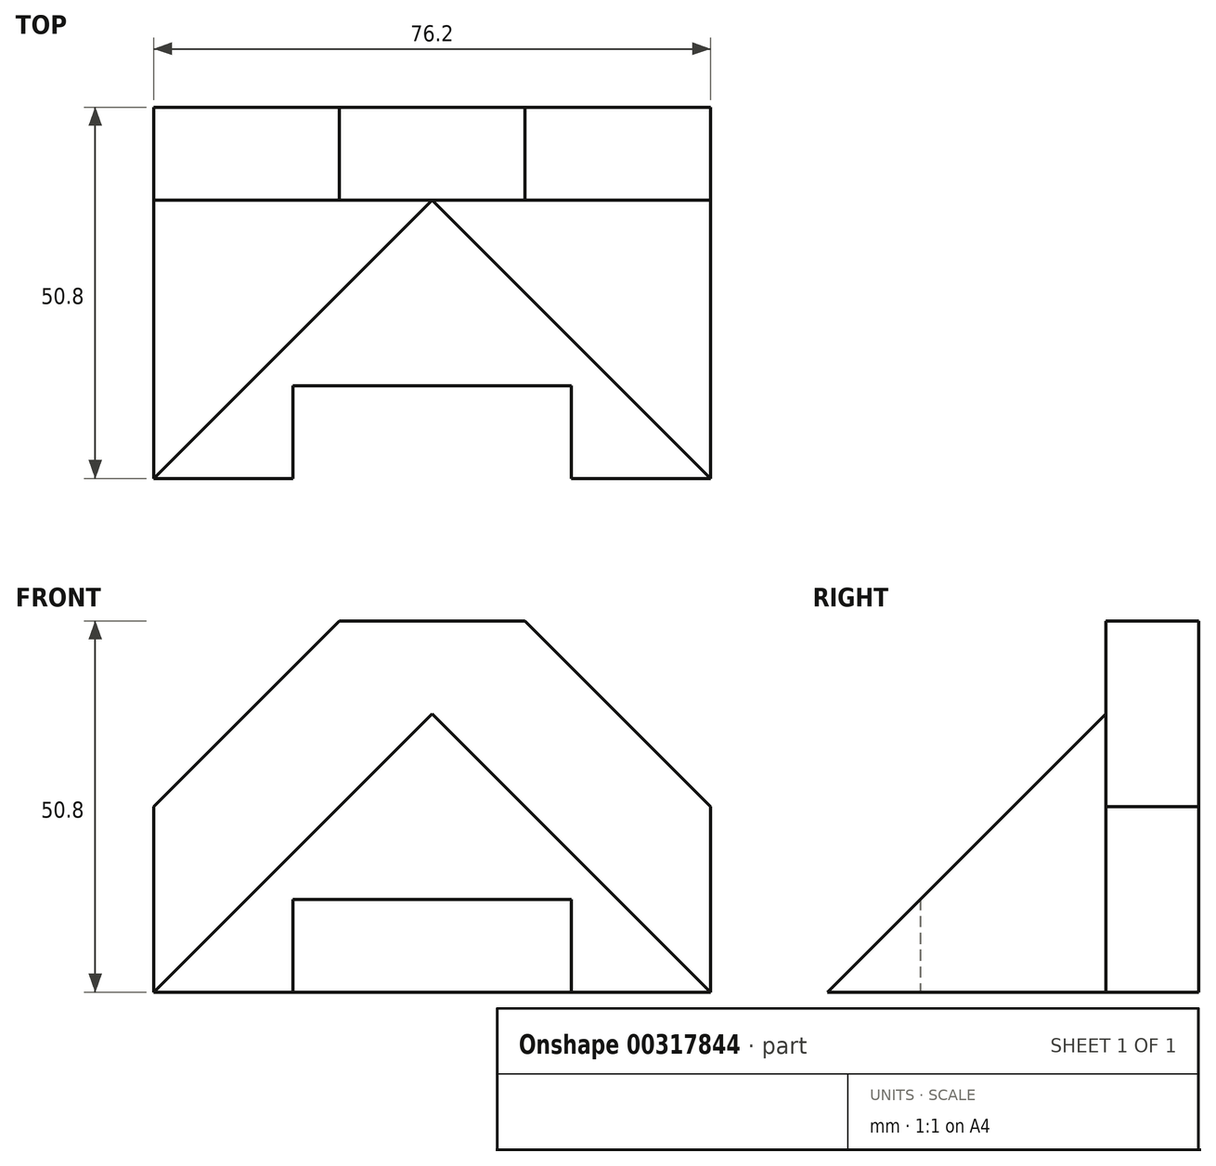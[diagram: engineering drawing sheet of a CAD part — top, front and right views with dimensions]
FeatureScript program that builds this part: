
annotation { "Feature Type Name" : "Feature", "Feature Type Description" : "" }
export const myFeature = defineFeature(function(context is Context, id is Id, definition is map)
    precondition{}
    {
        {
            var Q0;
            Q0=qCreatedBy(makeId("Front.planeOp"),FACE);
            var sketch = newSketch(context, id + "F0", { "sketchPlane" : qUnion([Q0])});
            skLineSegment(sketch, "E0.bottom", {"start": v(0, 0) * mm, "end": v(76.2, 0) * mm});
            skLineSegment(sketch, "E0.top", {"start": v(0, 50.8) * mm, "end": v(76.2, 50.8) * mm});
            skLineSegment(sketch, "E0.left", {"start": v(0, 0) * mm, "end": v(0, 50.8) * mm});
            skLineSegment(sketch, "E0.right", {"start": v(76.2, 0) * mm, "end": v(76.2, 50.8) * mm});
            skSolve(sketch);
        }
        {
            var Q0;
            Q0 = qSketchRegion(id + "F0", true);
            extrude(context, id + "F1", {"entities" : qUnion([Q0]), "oppositeDirection" : true, "depth" : 12.7 * mm});
        }
        {
            var Q0;
            Q0=qCreatedBy(makeId("Front.planeOp"),FACE);
            var sketch = newSketch(context, id + "F2", { "sketchPlane" : qUnion([Q0])});
            skLineSegment(sketch, "E1", {"start": v(0, 0) * mm, "end": v(0, 38.1) * mm});
            skLineSegment(sketch, "E2", {"start": v(0, 38.1) * mm, "end": v(76.2, 38.1) * mm});
            skLineSegment(sketch, "E3", {"start": v(76.2, 38.1) * mm, "end": v(76.2, 0) * mm});
            skLineSegment(sketch, "E4", {"start": v(76.2, 0) * mm, "end": v(0, 0) * mm});
            skSolve(sketch);
        }
        {
            var Q0;
            Q0 = qSketchRegion(id + "F2", true);
            extrude(context, id + "F3", {"entities" : qUnion([Q0]), "operationType" : NewBodyOperationType.ADD, "depth" : 38.1 * mm});
        }
        {
            var Q0;
            Q0=qCreatedBy(makeId("Right.planeOp"),FACE);
            var sketch = newSketch(context, id + "F4", { "sketchPlane" : qUnion([Q0])});
            skLineSegment(sketch, "E5", {"start": v(-38.1, 0) * mm, "end": v(0, 38.1) * mm});
            skLineSegment(sketch, "E6", {"start": v(0, 38.1) * mm, "end": v(-38.1, 38.1) * mm});
            skLineSegment(sketch, "E7", {"start": v(-38.1, 38.1) * mm, "end": v(-38.1, 0) * mm});
            skSolve(sketch);
        }
        {
            var Q0;
            Q0=makeQuery(id+"F3.opExtrude","CAP_FACE",FACE,{"disambiguationData":[OSD([sQuery(id+"F2.wireOp",EDGE,"E1"),sQuery(id+"F2.wireOp",EDGE,"E2"),sQuery(id+"F2.wireOp",EDGE,"E3"),sQuery(id+"F2.wireOp",EDGE,"E4")])],"isStart":false});
            var sketch = newSketch(context, id + "F5", { "sketchPlane" : qUnion([Q0])});
            skLineSegment(sketch, "E8", {"start": v(0, 0) * mm, "end": v(38.1, 38.1) * mm});
            skLineSegment(sketch, "E9", {"start": v(38.1, 38.1) * mm, "end": v(0, 38.1) * mm});
            skLineSegment(sketch, "E10", {"start": v(0, 38.1) * mm, "end": v(0, 0) * mm});
            skLineSegment(sketch, "E11", {"start": v(38.1, 66.18) * mm, "end": v(38.1, -28.88) * mm, "construction": true});
            skPoint(sketch, "E11.endSnap0", {"position": v(38.1, 0) * mm});
            skLineSegment(sketch, "E12.MirrorCS", {"start": v(38.1, 38.1) * mm, "end": v(76.2, 38.1) * mm});
            skLineSegment(sketch, "E13.MirrorCS", {"start": v(76.2, 0) * mm, "end": v(38.1, 38.1) * mm});
            skSolve(sketch);
        }
        {
            var Q0;
            Q0 = qSketchRegion(id + "F5", true);
            var Q1;
            Q1=makeQuery(id+"F5.imprint","IMPRINT",FACE,{"disambiguationData":[TD([[makeQuery(id+"F5.imprint","IMPRINT",EDGE,{"derivedFrom":sQuery(id+"F5.wireOp",EDGE,"E12.MirrorCS")}),-1.0]])]});
            extrude(context, id + "F6", {"entities" : qUnion([Q0, Q1]), "operationType" : NewBodyOperationType.REMOVE, "oppositeDirection" : true, "depth" : 38.1 * mm});
        }
        {
            var Q0;
            Q0 = qSketchRegion(id + "F4", true);
            extrude(context, id + "F7", {"entities" : qUnion([Q0]), "operationType" : NewBodyOperationType.REMOVE, "endBound" : BoundingType.THROUGH_ALL, "depth" : 25.4 * mm});
        }
        {
            var Q0;
            Q0=qCreatedBy(makeId("Top.planeOp"),FACE);
            var sketch = newSketch(context, id + "F8", { "sketchPlane" : qUnion([Q0])});
            skLineSegment(sketch, "E14.bottom", {"start": v(19.05, -25.4) * mm, "end": v(57.15, -25.4) * mm});
            skLineSegment(sketch, "E14.top", {"start": v(19.05, -38.1) * mm, "end": v(57.15, -38.1) * mm});
            skLineSegment(sketch, "E14.left", {"start": v(19.05, -25.4) * mm, "end": v(19.05, -38.1) * mm});
            skLineSegment(sketch, "E14.right", {"start": v(57.15, -25.4) * mm, "end": v(57.15, -38.1) * mm});
            skSolve(sketch);
        }
        {
            var Q0;
            Q0 = qSketchRegion(id + "F8", true);
            extrude(context, id + "F9", {"entities" : qUnion([Q0]), "operationType" : NewBodyOperationType.REMOVE, "endBound" : BoundingType.THROUGH_ALL, "depth" : 25.4 * mm});
        }
        {
            var Q0;
            Q0=qCreatedBy(makeId("Front.planeOp"),FACE);
            var sketch = newSketch(context, id + "F10", { "sketchPlane" : qUnion([Q0])});
            skLineSegment(sketch, "E15", {"start": v(0, 50.8) * mm, "end": v(0, 25.4) * mm});
            skLineSegment(sketch, "E16", {"start": v(0, 25.4) * mm, "end": v(25.4, 50.8) * mm});
            skLineSegment(sketch, "E17", {"start": v(25.4, 50.8) * mm, "end": v(0, 50.8) * mm});
            skLineSegment(sketch, "E18", {"start": v(50.8, 50.8) * mm, "end": v(76.2, 50.8) * mm});
            skLineSegment(sketch, "E19", {"start": v(76.2, 50.8) * mm, "end": v(76.2, 25.4) * mm});
            skLineSegment(sketch, "E20", {"start": v(76.2, 25.4) * mm, "end": v(50.8, 50.8) * mm});
            skSolve(sketch);
        }
        {
            var Q0;
            Q0 = qSketchRegion(id + "F10", true);
            extrude(context, id + "F11", {"entities" : qUnion([Q0]), "operationType" : NewBodyOperationType.REMOVE, "endBound" : BoundingType.THROUGH_ALL, "oppositeDirection" : true, "depth" : 25.4 * mm});
        }
    });
